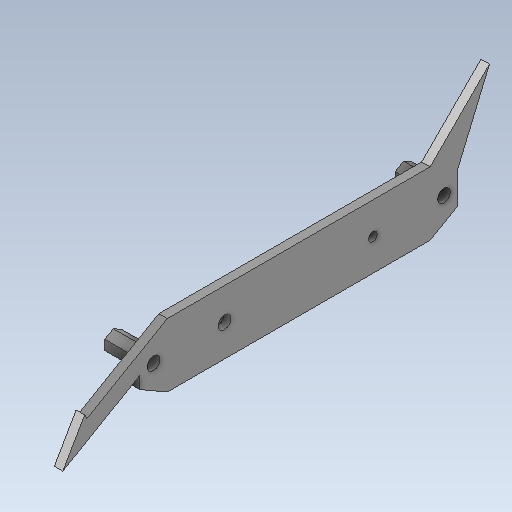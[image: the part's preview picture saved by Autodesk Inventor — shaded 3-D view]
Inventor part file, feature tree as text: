
AUTODESK INVENTOR PART (.ipt)
format: ipt  version: 2020 (Build 240168000, 168)  size: 176,128 bytes
history: native  units: in
note: dims shown in document units (in); Inventor stores cm internally (conversion verified against a paired STEP export)
features: other x3, extrude x2, sketch x2
ambient origin geometry x8: Origin, YZ Plane, XZ Plane, XY Plane, X Axis, Y Axis, Z Axis, Center Point
bodies: Solid1 (feature_tree)
feature tree (7):
  other  "HexWheelGuard.ipt"
  extrude  "Extrusion1"  Depth=0.315in
  extrude  "Extrusion2"  Depth=0.3937in
  other  "Solid1::HexWheelGuard.ipt"
  other  "TaggingFeature2"
  sketch  "Sketch1"  dims[d1=0.3937in d2=0.315in]
  sketch  "Sketch2"  dims[d3=60.0deg d4=1.4843in d5=0.0787in d6=0.3937in d7=0.0in d10=0.5906in d11=1.1024in d12=0.3937in d13=0.0in]
